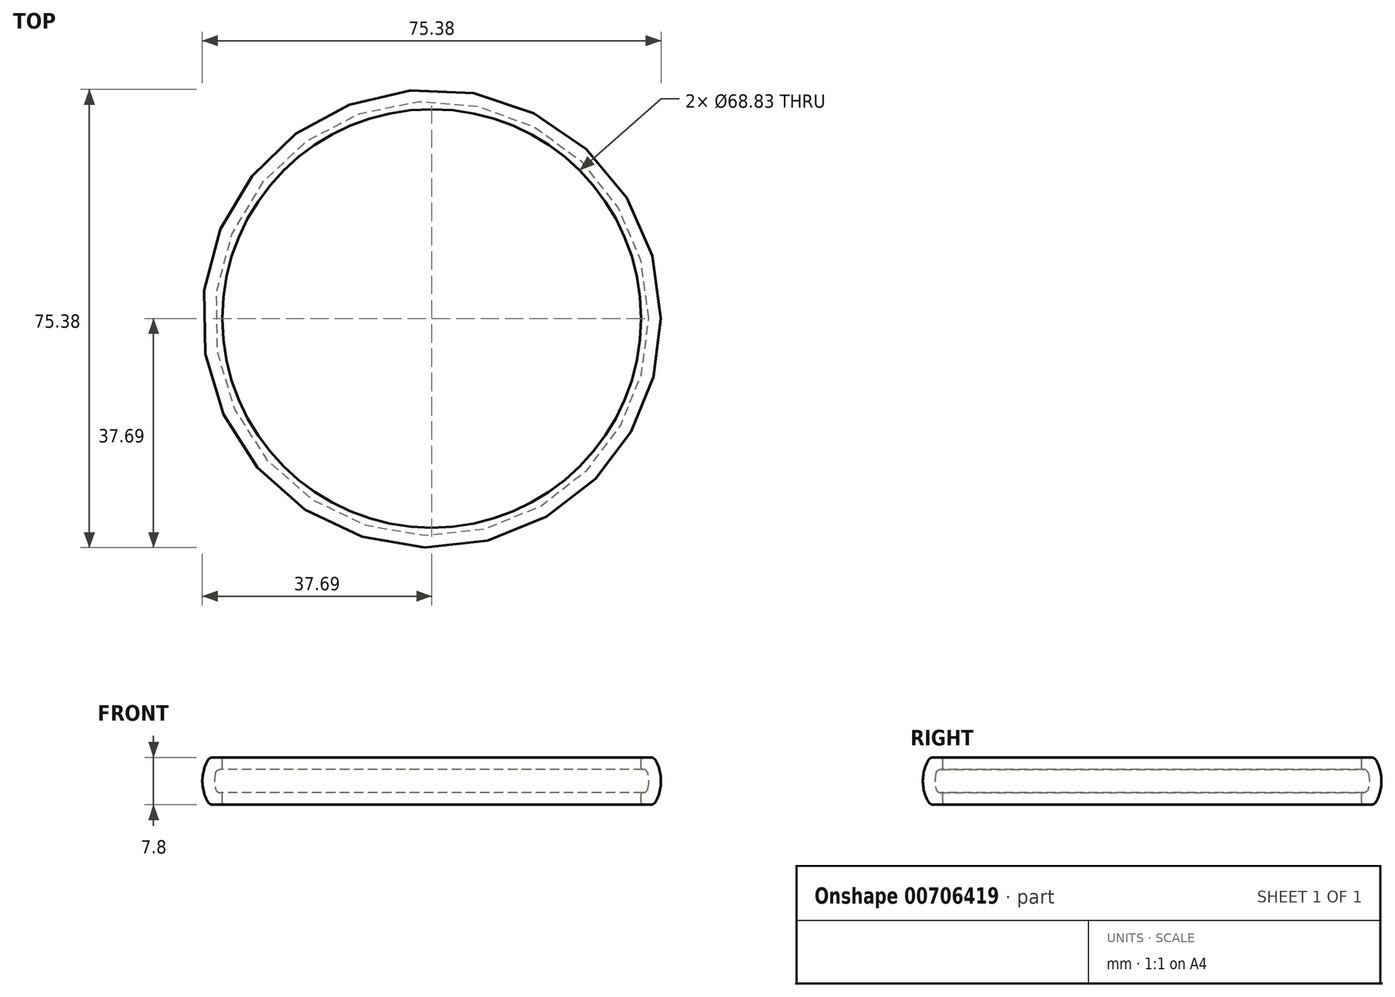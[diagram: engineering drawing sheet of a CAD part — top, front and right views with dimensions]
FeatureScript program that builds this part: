
annotation { "Feature Type Name" : "Feature", "Feature Type Description" : "" }
export const myFeature = defineFeature(function(context is Context, id is Id, definition is map)
    precondition{}
    {
        {
            var Q0;
            Q0=qCreatedBy(makeId("Front.planeOp"),FACE);
            var sketch = newSketch(context, id + "F0", { "sketchPlane" : qUnion([Q0])});
            skLineSegment(sketch, "E0", {"start": v(34.82, 3.9) * mm, "end": v(35.94, 3.9) * mm});
            skLineSegment(sketch, "E1", {"start": v(34.82, -3.9) * mm, "end": v(35.94, -3.9) * mm});
            skArc(sketch, "E2", {"start": v(36.82, -3.38) * mm, "mid": v(37.69, 0) * mm, "end": v(36.82, 3.38) * mm});
            skPoint(sketch, "E3.visualSharp", {"position": v(36.5, 3.9) * mm});
            skArc(sketch, "E3.filletArc", {"start": v(36.82, 3.38) * mm, "mid": v(36.45, 3.76) * mm, "end": v(35.94, 3.9) * mm});
            skPoint(sketch, "E4.visualSharp", {"position": v(36.5, -3.9) * mm});
            skArc(sketch, "E4.filletArc", {"start": v(35.94, -3.9) * mm, "mid": v(36.45, -3.76) * mm, "end": v(36.82, -3.38) * mm});
            skPoint(sketch, "E5.visualSharp", {"position": v(33.5, 3.9) * mm});
            skArc(sketch, "E5.filletArc", {"start": v(34.82, 3.9) * mm, "mid": v(34.53, 3.78) * mm, "end": v(34.42, 3.5) * mm});
            skPoint(sketch, "E6.visualSharp", {"position": v(33.5, -3.9) * mm});
            skArc(sketch, "E6.filletArc", {"start": v(34.42, -3.5) * mm, "mid": v(34.53, -3.78) * mm, "end": v(34.82, -3.9) * mm});
            skLineSegment(sketch, "E7.0", {"start": v(34.78, -1.9) * mm, "end": v(41, -1.9) * mm});
            skLineSegment(sketch, "E7.2", {"start": v(34.78, 1.9) * mm, "end": v(40.83, 1.9) * mm});
            skArc(sketch, "E7.3", {"start": v(35.5, -1.35) * mm, "mid": v(35.69, 0) * mm, "end": v(35.5, 1.35) * mm});
            skPoint(sketch, "E8.visualSharp", {"position": v(35.31, 1.9) * mm});
            skArc(sketch, "E8.filletArc", {"start": v(35.5, 1.35) * mm, "mid": v(35.23, 1.75) * mm, "end": v(34.78, 1.9) * mm});
            skPoint(sketch, "E9.visualSharp", {"position": v(35.31, -1.9) * mm});
            skArc(sketch, "E9.filletArc", {"start": v(34.78, -1.9) * mm, "mid": v(35.23, -1.75) * mm, "end": v(35.5, -1.35) * mm});
            skLineSegment(sketch, "E10", {"start": v(41, 1.9) * mm, "end": v(34.72, 1.9) * mm});
            skLineSegment(sketch, "E11", {"start": v(34.72, -1.9) * mm, "end": v(41, -1.9) * mm});
            skLineSegment(sketch, "E12", {"start": v(34.42, 2.2) * mm, "end": v(34.42, 3.5) * mm});
            skLineSegment(sketch, "E13", {"start": v(34.42, -2.2) * mm, "end": v(34.42, -3.5) * mm});
            skPoint(sketch, "E14.visualSharp", {"position": v(34.42, 1.9) * mm});
            skArc(sketch, "E14.filletArc", {"start": v(34.42, 2.2) * mm, "mid": v(34.5, 1.99) * mm, "end": v(34.72, 1.9) * mm});
            skPoint(sketch, "E15.visualSharp", {"position": v(34.42, -1.9) * mm});
            skArc(sketch, "E15.filletArc", {"start": v(34.72, -1.9) * mm, "mid": v(34.5, -1.99) * mm, "end": v(34.42, -2.2) * mm});
            skSolve(sketch);
        }
        {
            var Q0;
            Q0=qCreatedBy(makeId("Front.planeOp"),FACE);
            var sketch = newSketch(context, id + "F1", { "sketchPlane" : qUnion([Q0])});
            skLineSegment(sketch, "E16", {"start": v(0, 43.52) * mm, "end": v(0, -40.69) * mm});
            skSolve(sketch);
        }
        {
            var Q0;
            Q0 = qSketchRegion(id + "F0", true);
            var Q1;
            Q1=sQuery(id+"F1.wireOp",EDGE,"E16");
            revolve(context, id + "F2", {"surfaceOperationType" : NewSurfaceOperationType.NEW, "entities" : qUnion([Q0]), "axis" : qUnion([Q1]), "revolveType" : RevolveType.FULL});
        }
    });
